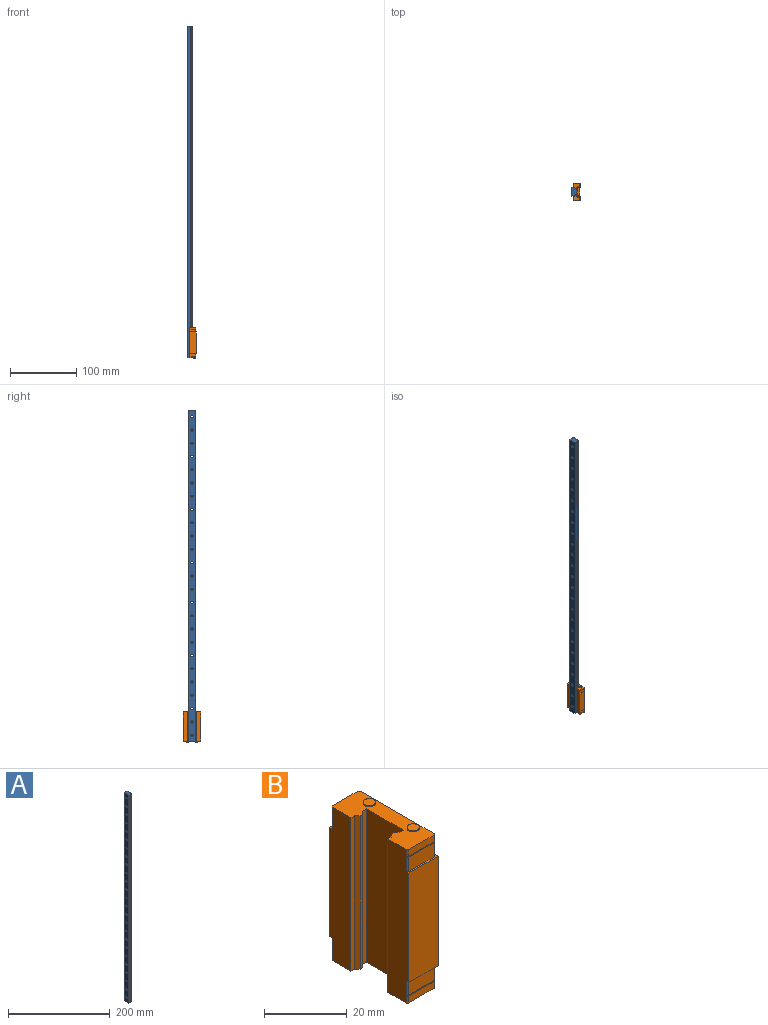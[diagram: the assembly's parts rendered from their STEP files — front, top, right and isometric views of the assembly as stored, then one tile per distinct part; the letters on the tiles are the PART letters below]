
ASSEMBLY  parts=2 mates=1
PART A: 89 faces, bbox 8x12x500 mm
  f0: plane 500x12mm, normal (1,0,0), area 5293.1mm2, adj f10,f11,f13,f15,f18,f21,f24,f27
  f1: cylinder r=1.75mm len=5.5mm, axis (-1,0,0), area 60.5mm2, adj f5,f14
  f2: plane 500x1mm, normal (0,1,0), area 500mm2, adj f3,f11,f12,f86
  f3: plane 500x1mm, normal (0.71,0.71,0), area 707.1mm2, adj f2,f4,f11,f86
  f4: plane 500x4mm, normal (0,1,0), area 2000mm2, adj f3,f5,f11,f86
  f5: plane 500x12mm, normal (-1,0,0), area 5759.5mm2, adj f1,f4,f6,f11,f16,f19,f22,f25
  f6: plane 500x4mm, normal (0,-1,0), area 2000mm2, adj f5,f7,f11,f86
  f7: plane 500x1mm, normal (0.71,-0.71,0), area 707.1mm2, adj f6,f8,f11,f86
  f8: plane 500x1mm, normal (0,-1,0), area 500mm2, adj f7,f9,f11,f86
  f9: plane 500x1mm, normal (-0.71,-0.71,0), area 707.1mm2, adj f8,f10,f11,f86
  f10: plane 500x1mm, normal (0,-1,0), area 500mm2, adj f0,f9,f11,f86
  f11: plane 12x8mm, normal (0,0,-1), area 92mm2, adj f0,f2,f3,f4,f5,f6,f7,f8
  f12: plane 500x1mm, normal (-0.71,0.71,0), area 707.1mm2, adj f2,f11,f13,f86
  f13: plane 500x1mm, normal (0,1,0), area 500mm2, adj f0,f11,f12,f86
  f14: plane 6x6mm, normal (1,0,0), area 18.7mm2, adj f1,f15
  f15: cylinder r=3mm len=6mm, axis (-1,0,0), area 47.1mm2, adj f0,f14
  f16: cylinder r=1.75mm len=5.5mm, axis (-1,0,0), area 60.5mm2, adj f5,f17
  f17: plane 6x6mm, normal (1,0,0), area 18.7mm2, adj f16,f18
  f18: cylinder r=3mm len=6mm, axis (-1,0,0), area 47.1mm2, adj f0,f17
  f19: cylinder r=1.75mm len=5.5mm, axis (-1,0,0), area 60.5mm2, adj f5,f20
  f20: plane 6x6mm, normal (1,0,0), area 18.7mm2, adj f19,f21
  f21: cylinder r=3mm len=6mm, axis (-1,0,0), area 47.1mm2, adj f0,f20
  f22: cylinder r=1.75mm len=5.5mm, axis (-1,0,0), area 60.5mm2, adj f5,f23
  f23: plane 6x6mm, normal (1,0,0), area 18.7mm2, adj f22,f24
  f24: cylinder r=3mm len=6mm, axis (-1,0,0), area 47.1mm2, adj f0,f23
  f25: cylinder r=1.75mm len=5.5mm, axis (-1,0,0), area 60.5mm2, adj f5,f26
  f26: plane 6x6mm, normal (1,0,0), area 18.7mm2, adj f25,f27
  f27: cylinder r=3mm len=6mm, axis (-1,0,0), area 47.1mm2, adj f0,f26
  f28: cylinder r=1.75mm len=5.5mm, axis (-1,0,0), area 60.5mm2, adj f5,f29
  f29: plane 6x6mm, normal (1,0,0), area 18.7mm2, adj f28,f30
  f30: cylinder r=3mm len=6mm, axis (-1,0,0), area 47.1mm2, adj f0,f29
  f31: cylinder r=1.75mm len=5.5mm, axis (-1,0,0), area 60.5mm2, adj f5,f32
  f32: plane 6x6mm, normal (1,0,0), area 18.7mm2, adj f31,f33
  f33: cylinder r=3mm len=6mm, axis (-1,0,0), area 47.1mm2, adj f0,f32
  f34: cylinder r=1.75mm len=5.5mm, axis (-1,0,0), area 60.5mm2, adj f5,f35
  f35: plane 6x6mm, normal (1,0,0), area 18.7mm2, adj f34,f36
  f36: cylinder r=3mm len=6mm, axis (-1,0,0), area 47.1mm2, adj f0,f35
  f37: cylinder r=1.75mm len=5.5mm, axis (-1,0,0), area 60.5mm2, adj f5,f38
  f38: plane 6x6mm, normal (1,0,0), area 18.7mm2, adj f37,f39
  f39: cylinder r=3mm len=6mm, axis (-1,0,0), area 47.1mm2, adj f0,f38
  f40: cylinder r=1.75mm len=5.5mm, axis (-1,0,0), area 60.5mm2, adj f5,f41
  f41: plane 6x6mm, normal (1,0,0), area 18.7mm2, adj f40,f42
  f42: cylinder r=3mm len=6mm, axis (-1,0,0), area 47.1mm2, adj f0,f41
  f43: cylinder r=1.75mm len=5.5mm, axis (-1,0,0), area 60.5mm2, adj f5,f44
  f44: plane 6x6mm, normal (1,0,0), area 18.7mm2, adj f43,f45
  f45: cylinder r=3mm len=6mm, axis (-1,0,0), area 47.1mm2, adj f0,f44
  f46: cylinder r=1.75mm len=5.5mm, axis (-1,0,0), area 60.5mm2, adj f5,f47
  f47: plane 6x6mm, normal (1,0,0), area 18.7mm2, adj f46,f48
  f48: cylinder r=3mm len=6mm, axis (-1,0,0), area 47.1mm2, adj f0,f47
  f49: cylinder r=1.75mm len=5.5mm, axis (-1,0,0), area 60.5mm2, adj f5,f50
  f50: plane 6x6mm, normal (1,0,0), area 18.7mm2, adj f49,f51
  f51: cylinder r=3mm len=6mm, axis (-1,0,0), area 47.1mm2, adj f0,f50
  f52: cylinder r=1.75mm len=5.5mm, axis (-1,0,0), area 60.5mm2, adj f5,f53
  f53: plane 6x6mm, normal (1,0,0), area 18.7mm2, adj f52,f54
  f54: cylinder r=3mm len=6mm, axis (-1,0,0), area 47.1mm2, adj f0,f53
  f55: cylinder r=1.75mm len=5.5mm, axis (-1,0,0), area 60.5mm2, adj f5,f56
  f56: plane 6x6mm, normal (1,0,0), area 18.7mm2, adj f55,f57
  f57: cylinder r=3mm len=6mm, axis (-1,0,0), area 47.1mm2, adj f0,f56
  f58: cylinder r=1.75mm len=5.5mm, axis (-1,0,0), area 60.5mm2, adj f5,f59
  f59: plane 6x6mm, normal (1,0,0), area 18.7mm2, adj f58,f60
  f60: cylinder r=3mm len=6mm, axis (-1,0,0), area 47.1mm2, adj f0,f59
  f61: cylinder r=1.75mm len=5.5mm, axis (-1,0,0), area 60.5mm2, adj f5,f62
  f62: plane 6x6mm, normal (1,0,0), area 18.7mm2, adj f61,f63
  f63: cylinder r=3mm len=6mm, axis (-1,0,0), area 47.1mm2, adj f0,f62
  f64: cylinder r=1.75mm len=5.5mm, axis (-1,0,0), area 60.5mm2, adj f5,f65
  f65: plane 6x6mm, normal (1,0,0), area 18.7mm2, adj f64,f66
  f66: cylinder r=3mm len=6mm, axis (-1,0,0), area 47.1mm2, adj f0,f65
  f67: cylinder r=1.75mm len=5.5mm, axis (-1,0,0), area 60.5mm2, adj f5,f68
  f68: plane 6x6mm, normal (1,0,0), area 18.7mm2, adj f67,f69
  f69: cylinder r=3mm len=6mm, axis (-1,0,0), area 47.1mm2, adj f0,f68
  f70: cylinder r=1.75mm len=5.5mm, axis (-1,0,0), area 60.5mm2, adj f5,f71
  f71: plane 6x6mm, normal (1,0,0), area 18.7mm2, adj f70,f72
  f72: cylinder r=3mm len=6mm, axis (-1,0,0), area 47.1mm2, adj f0,f71
  f73: cylinder r=1.75mm len=5.5mm, axis (-1,0,0), area 60.5mm2, adj f5,f74
  f74: plane 6x6mm, normal (1,0,0), area 18.7mm2, adj f73,f75
  f75: cylinder r=3mm len=6mm, axis (-1,0,0), area 47.1mm2, adj f0,f74
  f76: cylinder r=1.75mm len=5.5mm, axis (-1,0,0), area 60.5mm2, adj f5,f77
  f77: plane 6x6mm, normal (1,0,0), area 18.7mm2, adj f76,f78
  f78: cylinder r=3mm len=6mm, axis (-1,0,0), area 47.1mm2, adj f0,f77
  f79: cylinder r=1.75mm len=5.5mm, axis (-1,0,0), area 60.5mm2, adj f5,f80
  f80: plane 6x6mm, normal (1,0,0), area 18.7mm2, adj f79,f81
  f81: cylinder r=3mm len=6mm, axis (-1,0,0), area 47.1mm2, adj f0,f80
  f82: cylinder r=1.75mm len=5.5mm, axis (-1,0,0), area 60.5mm2, adj f5,f83
  f83: plane 6x6mm, normal (1,0,0), area 18.7mm2, adj f82,f84
  f84: cylinder r=3mm len=6mm, axis (-1,0,0), area 47.1mm2, adj f0,f83
  f85: cylinder r=1.75mm len=5.5mm, axis (-1,0,0), area 60.5mm2, adj f5,f87
  f86: plane 12x8mm, normal (0,0,1), area 92mm2, adj f0,f2,f3,f4,f5,f6,f7,f8
  f87: plane 6x6mm, normal (1,0,0), area 18.7mm2, adj f85,f88
  f88: cylinder r=3mm len=6mm, axis (-1,0,0), area 47.1mm2, adj f0,f87
PART B: 82 faces, bbox 10x27x46 mm
  f0: plane 25.29x3.9mm, normal (1,0,0), area 98.6mm2, adj f19,f48,f53,f61
  f1: plane 32.4x13mm, normal (1,0,0), area 421.2mm2, adj f21,f24,f25,f38
  f2: plane 25.29x3.9mm, normal (1,0,0), area 98.6mm2, adj f12,f13,f58,f63
  f3: plane 25.29x2mm, normal (1,0,0), area 50.6mm2, adj f11,f14,f42,f56
  f4: plane 25.29x2mm, normal (1,0,0), area 50.6mm2, adj f18,f45,f49,f55
  f5: plane 8.79x4.2mm, normal (0,1,0), area 36.9mm2, adj f10,f12,f38,f58
  f6: plane 8.79x4.2mm, normal (0,-1,0), area 36.9mm2, adj f13,f15,f38,f58
  f7: plane 8.79x2mm, normal (0,-1,0), area 17.6mm2, adj f17,f18,f45,f55
  f8: plane 8.79x2mm, normal (0,1,0), area 17.6mm2, adj f45,f49,f51,f55
  f9: plane 2x0.35mm, normal (-0.71,0.71,0), area 1mm2, adj f28,f42,f43,f56
  f10: plane 4.2x0.35mm, normal (-0.71,0.71,0), area 2.1mm2, adj f5,f28,f38,f58
  f11: plane 2x0.35mm, normal (0.71,0.71,0), area 1mm2, adj f3,f42,f43,f56
  f12: plane 4.2x0.35mm, normal (0.71,0.71,0), area 2mm2, adj f2,f5,f38,f58,f63,f64
  f13: plane 4.2x0.35mm, normal (0.71,-0.71,0), area 2mm2, adj f2,f6,f38,f58,f63,f64
  f14: plane 2x0.35mm, normal (0.71,-0.71,0), area 1mm2, adj f3,f42,f44,f56
  f15: plane 4.2x0.35mm, normal (-0.71,-0.71,0), area 2.1mm2, adj f6,f38,f40,f58
  f16: plane 2x0.35mm, normal (-0.71,-0.71,0), area 1mm2, adj f40,f42,f44,f56
  f17: plane 2x0.35mm, normal (-0.71,-0.71,0), area 1mm2, adj f7,f40,f45,f55
  f18: plane 2x0.35mm, normal (0.71,-0.71,0), area 1mm2, adj f4,f7,f45,f55
  f19: plane 4.2x0.35mm, normal (0.71,0.71,0), area 2mm2, adj f0,f21,f50,f53,f60,f61
  f20: plane 4.2x0.35mm, normal (-0.71,0.71,0), area 2.1mm2, adj f21,f28,f50,f53
  f21: plane 27x10mm, normal (0,0,1), area 24.4mm2, adj f1,f19,f20,f22,f23,f24,f25,f26
  f22: plane 32.4x10mm, normal (0,-1,0), area 324mm2, adj f21,f23,f38,f40
  f23: plane 32.4x7mm, normal (1,0,0), area 212.7mm2, adj f21,f22,f24,f38,f79,f81
  f24: plane 32.4x0.5mm, normal (0,1,0), area 16.2mm2, adj f1,f21,f23,f38
  f25: plane 32.4x0.5mm, normal (0,-1,0), area 16.2mm2, adj f1,f21,f26,f38
  f26: plane 32.4x7mm, normal (1,0,0), area 212.7mm2, adj f21,f25,f27,f38,f75,f77
  f27: plane 32.4x10mm, normal (0,1,0), area 324mm2, adj f21,f26,f28,f38
  f28: plane 45.4x7.2mm, normal (-1,0,0), area 315.8mm2, adj f9,f10,f20,f21,f27,f29,f38,f42
  f29: plane 45.4x1.12mm, normal (0,-1,0), area 51mm2, adj f28,f30,f42,f45
  f30: plane 45.4x1mm, normal (-0.71,-0.71,0), area 64.2mm2, adj f29,f31,f42,f45
  f31: plane 45.4x0.75mm, normal (0,-1,0), area 34.1mm2, adj f30,f32,f42,f45
  f32: plane 45.4x1mm, normal (0.71,-0.71,0), area 64.2mm2, adj f31,f33,f42,f45
  f33: plane 45.4x1.42mm, normal (0,-1,0), area 64.7mm2, adj f32,f34,f42,f45
  f34: plane 45.4x12.6mm, normal (-1,0,0), area 572mm2, adj f33,f35,f42,f45
  f35: plane 45.4x1.42mm, normal (0,1,0), area 64.7mm2, adj f34,f36,f42,f45
  f36: plane 45.4x1mm, normal (0.71,0.71,0), area 64.2mm2, adj f35,f37,f42,f45
  f37: plane 45.4x0.75mm, normal (0,1,0), area 34.1mm2, adj f36,f39,f42,f45
  f38: plane 27x10mm, normal (0,0,-1), area 24.4mm2, adj f1,f5,f6,f10,f12,f13,f15,f22
  f39: plane 45.4x1mm, normal (-0.71,0.71,0), area 64.2mm2, adj f37,f41,f42,f45
  f40: plane 45.4x7.2mm, normal (-1,0,0), area 315.8mm2, adj f15,f16,f17,f21,f22,f38,f41,f42
  f41: plane 45.4x1.12mm, normal (0,1,0), area 51mm2, adj f39,f40,f42,f45
  f42: plane 26x9.5mm, normal (0,0,-1), area 169.3mm2, adj f3,f9,f11,f14,f16,f28,f29,f30
  f43: plane 8.79x2mm, normal (0,1,0), area 17.6mm2, adj f9,f11,f42,f56
  f44: plane 8.79x2mm, normal (0,-1,0), area 17.6mm2, adj f14,f16,f42,f56
  f45: plane 26x9.5mm, normal (0,0,1), area 169.3mm2, adj f4,f7,f8,f17,f18,f28,f29,f30
  f46: plane 4.2x0.35mm, normal (-0.71,-0.71,0), area 2.1mm2, adj f21,f40,f47,f53
  f47: plane 8.79x4.2mm, normal (0,-1,0), area 36.9mm2, adj f21,f46,f48,f53
  f48: plane 4.2x0.35mm, normal (0.71,-0.71,0), area 2mm2, adj f0,f21,f47,f53,f60,f61
  f49: plane 2x0.35mm, normal (0.71,0.71,0), area 1mm2, adj f4,f8,f45,f55
  f50: plane 8.79x4.2mm, normal (0,1,0), area 36.9mm2, adj f19,f20,f21,f53
  f51: plane 2x0.35mm, normal (-0.71,0.71,0), area 1mm2, adj f8,f28,f45,f55
  f52: plane 9.2x0.3mm, normal (0,1,0), area 2.8mm2, adj f28,f53,f55,f65
  f53: plane 26x9.5mm, normal (0,0,1), area 14.1mm2, adj f0,f19,f20,f46,f47,f48,f50,f52
  f54: plane 9.2x0.3mm, normal (0,-1,0), area 2.8mm2, adj f40,f53,f55,f65
  f55: plane 26x9.5mm, normal (0,0,-1), area 14.1mm2, adj f4,f7,f8,f17,f18,f49,f51,f52
  f56: plane 26x9.5mm, normal (0,0,1), area 14.1mm2, adj f3,f9,f11,f14,f16,f43,f44,f57
  f57: plane 9.2x0.3mm, normal (0,-1,0), area 2.8mm2, adj f40,f56,f58,f62
  f58: plane 26x9.5mm, normal (0,0,-1), area 14.1mm2, adj f2,f5,f6,f10,f12,f13,f15,f57
  f59: plane 9.2x0.3mm, normal (0,1,0), area 2.8mm2, adj f28,f56,f58,f62
  f60: plane 25.89x0.3mm, normal (1,0,0), area 7.8mm2, adj f19,f21,f48,f61
  f61: plane 25.89x0.3mm, normal (0,0,-1), area 7.7mm2, adj f0,f19,f48,f60
  f62: plane 25.29x0.3mm, normal (1,0,0), area 7.6mm2, adj f56,f57,f58,f59
  f63: plane 25.89x0.3mm, normal (0,0,1), area 7.7mm2, adj f2,f12,f13,f64
  f64: plane 25.89x0.3mm, normal (1,0,0), area 7.8mm2, adj f12,f13,f38,f63
  f65: plane 25.29x0.3mm, normal (1,0,0), area 7.6mm2, adj f52,f53,f54,f55
  f66: plane 3x3mm, normal (0,0,1), area 7.1mm2, adj f67
  f67: cylinder r=1.5mm len=3mm, axis (0,0,-1), area 2.8mm2, adj f45,f66
  f68: cylinder r=1.5mm len=3mm, axis (0,0,-1), area 2.8mm2, adj f42,f69
  f69: plane 3x3mm, normal (0,0,-1), area 7.1mm2, adj f68
  f70: plane 3x3mm, normal (0,0,1), area 7.1mm2, adj f71
  f71: cylinder r=1.5mm len=3mm, axis (0,0,-1), area 2.8mm2, adj f45,f70
  f72: cylinder r=1.5mm len=3mm, axis (0,0,-1), area 2.8mm2, adj f42,f73
  f73: plane 3x3mm, normal (0,0,-1), area 7.1mm2, adj f72
  f74: plane 3x3mm, normal (1,0,0), area 7.1mm2, adj f75
  f75: cylinder r=1.5mm len=3.5mm, axis (-1,0,0), area 33mm2, adj f26,f74
  f76: plane 3x3mm, normal (1,0,0), area 7.1mm2, adj f77
  f77: cylinder r=1.5mm len=3.5mm, axis (-1,0,0), area 33mm2, adj f26,f76
  f78: plane 3x3mm, normal (1,0,0), area 7.1mm2, adj f79
  f79: cylinder r=1.5mm len=3.5mm, axis (-1,0,0), area 33mm2, adj f23,f78
  f80: plane 3x3mm, normal (1,0,0), area 7.1mm2, adj f81
  f81: cylinder r=1.5mm len=3.5mm, axis (-1,0,0), area 33mm2, adj f23,f80
PLACE A at identity fixed
PLACE B t=(0,42,22.7)mm
MATE slider B.f42 <-> A.f11  axis (0,0,-1) through (8.3,20,0)mm
